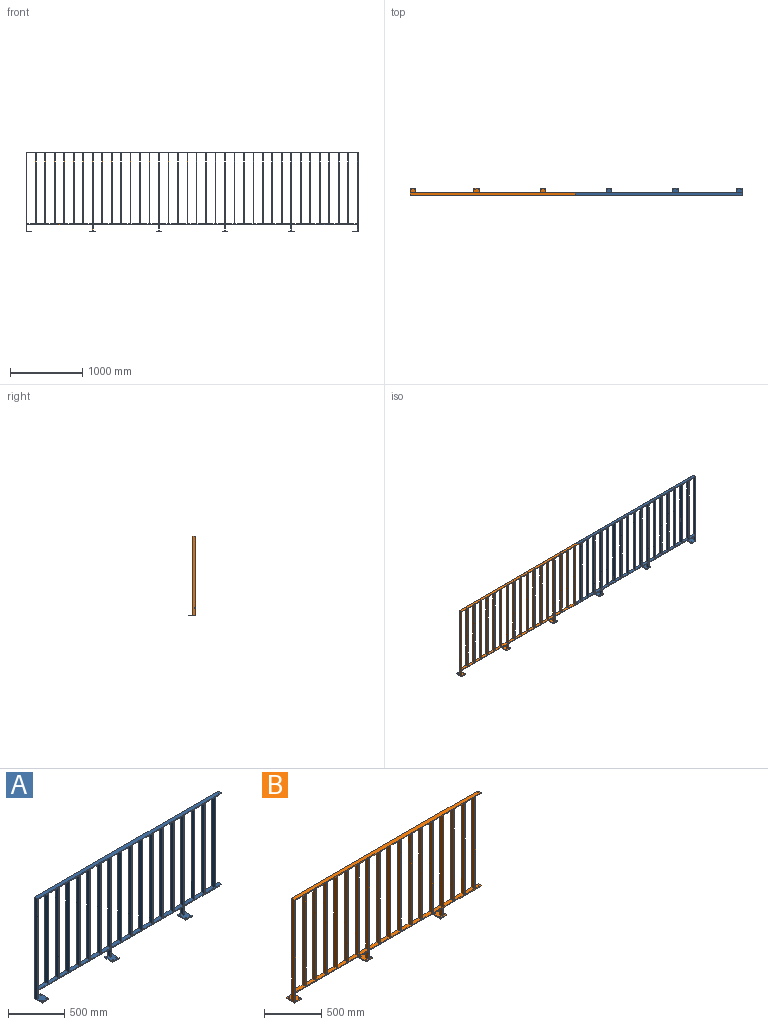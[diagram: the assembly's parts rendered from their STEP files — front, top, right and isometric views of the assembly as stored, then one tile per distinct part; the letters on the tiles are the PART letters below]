
ASSEMBLY  parts=2 mates=1
PART A: 114 faces, bbox 2304x100x1100 mm
  f0: plane 2304x1100mm, normal (0,1,0), area 227330mm2, adj f1,f2,f3,f4,f5,f6,f7,f8
  f1: plane 438x40mm, normal (0,0,-1), area 17520mm2, adj f0,f22,f83,f87
  f2: plane 906x40mm, normal (0,0,-1), area 36240mm2, adj f0,f22,f81,f84
  f3: plane 905x40mm, normal (0,0,-1), area 36200mm2, adj f0,f22,f80,f82
  f4: plane 120.8x40mm, normal (0,0,1), area 4832mm2, adj f0,f22,f58,f59
  f5: plane 120.8x40mm, normal (0,0,1), area 4832mm2, adj f0,f22,f56,f57
  f6: plane 120.8x40mm, normal (0,0,1), area 4832mm2, adj f0,f22,f54,f55
  f7: plane 120.8x40mm, normal (0,0,1), area 4832mm2, adj f0,f22,f52,f53
  f8: plane 120.8x40mm, normal (0,0,1), area 4832mm2, adj f0,f22,f48,f49
  f9: plane 120.8x40mm, normal (0,0,1), area 4832mm2, adj f0,f22,f46,f47
  f10: plane 120.8x40mm, normal (0,0,1), area 4832mm2, adj f0,f22,f44,f45
  f11: plane 120.8x40mm, normal (0,0,1), area 4832mm2, adj f0,f22,f42,f43
  f12: plane 120.8x40mm, normal (0,0,1), area 4832mm2, adj f0,f22,f40,f41
  f13: plane 120.8x40mm, normal (0,0,1), area 4832mm2, adj f0,f22,f38,f39
  f14: plane 120.8x40mm, normal (0,0,1), area 4832mm2, adj f0,f22,f36,f37
  f15: plane 120.8x40mm, normal (0,0,1), area 4832mm2, adj f0,f22,f34,f35
  f16: plane 120.8x40mm, normal (0,0,1), area 4832mm2, adj f0,f22,f25,f33
  f17: plane 70.4x40mm, normal (0,0,1), area 2816mm2, adj f0,f22,f23,f32
  f18: plane 120.8x40mm, normal (0,0,1), area 4832mm2, adj f0,f22,f30,f31
  f19: plane 120.8x40mm, normal (0,0,1), area 4832mm2, adj f0,f22,f28,f29
  f20: plane 120.8x40mm, normal (0,0,1), area 4832mm2, adj f0,f22,f26,f27
  f21: plane 1100x100mm, normal (-1,0,0), area 44600mm2, adj f0,f22,f78,f90,f91,f92
  f22: plane 2304x1090mm, normal (0,-1,0), area 224930mm2, adj f1,f2,f3,f4,f5,f6,f7,f8
  f23: plane 40x5mm, normal (1,0,0), area 200mm2, adj f0,f17,f22,f88
  f24: plane 120.8x40mm, normal (0,0,1), area 4832mm2, adj f0,f22,f50,f51
  f25: plane 980x40mm, normal (-1,0,0), area 39200mm2, adj f0,f16,f22,f60
  f26: plane 980x40mm, normal (1,0,0), area 39200mm2, adj f0,f20,f22,f61
  f27: plane 980x40mm, normal (-1,0,0), area 39200mm2, adj f0,f20,f22,f61
  f28: plane 980x40mm, normal (1,0,0), area 39200mm2, adj f0,f19,f22,f62
  f29: plane 980x40mm, normal (-1,0,0), area 39200mm2, adj f0,f19,f22,f62
  f30: plane 980x40mm, normal (1,0,0), area 39200mm2, adj f0,f18,f22,f63
  f31: plane 980x40mm, normal (-1,0,0), area 39200mm2, adj f0,f18,f22,f63
  f32: plane 980x40mm, normal (1,0,0), area 39200mm2, adj f0,f17,f22,f73
  f33: plane 980x40mm, normal (1,0,0), area 39200mm2, adj f0,f16,f22,f60
  f34: plane 980x40mm, normal (-1,0,0), area 39200mm2, adj f0,f15,f22,f64
  f35: plane 980x40mm, normal (1,0,0), area 39200mm2, adj f0,f15,f22,f64
  f36: plane 980x40mm, normal (-1,0,0), area 39200mm2, adj f0,f14,f22,f65
  f37: plane 980x40mm, normal (1,0,0), area 39200mm2, adj f0,f14,f22,f65
  f38: plane 980x40mm, normal (-1,0,0), area 39200mm2, adj f0,f13,f22,f66
  f39: plane 980x40mm, normal (1,0,0), area 39200mm2, adj f0,f13,f22,f66
  f40: plane 980x40mm, normal (-1,0,0), area 39200mm2, adj f0,f12,f22,f67
  f41: plane 980x40mm, normal (1,0,0), area 39200mm2, adj f0,f12,f22,f67
  f42: plane 980x40mm, normal (-1,0,0), area 39200mm2, adj f0,f11,f22,f68
  f43: plane 980x40mm, normal (1,0,0), area 39200mm2, adj f0,f11,f22,f68
  f44: plane 980x40mm, normal (-1,0,0), area 39200mm2, adj f0,f10,f22,f69
  f45: plane 980x40mm, normal (1,0,0), area 39200mm2, adj f0,f10,f22,f69
  f46: plane 980x40mm, normal (-1,0,0), area 39200mm2, adj f0,f9,f22,f70
  f47: plane 980x40mm, normal (1,0,0), area 39200mm2, adj f0,f9,f22,f70
  f48: plane 980x40mm, normal (-1,0,0), area 39200mm2, adj f0,f8,f22,f71
  f49: plane 980x40mm, normal (1,0,0), area 39200mm2, adj f0,f8,f22,f71
  f50: plane 980x40mm, normal (-1,0,0), area 39200mm2, adj f0,f22,f24,f72
  f51: plane 980x40mm, normal (1,0,0), area 39200mm2, adj f0,f22,f24,f72
  f52: plane 980x40mm, normal (-1,0,0), area 39200mm2, adj f0,f7,f22,f74
  f53: plane 980x40mm, normal (1,0,0), area 39200mm2, adj f0,f7,f22,f74
  f54: plane 980x40mm, normal (-1,0,0), area 39200mm2, adj f0,f6,f22,f75
  f55: plane 980x40mm, normal (1,0,0), area 39200mm2, adj f0,f6,f22,f75
  f56: plane 980x40mm, normal (-1,0,0), area 39200mm2, adj f0,f5,f22,f76
  f57: plane 980x40mm, normal (1,0,0), area 39200mm2, adj f0,f5,f22,f76
  f58: plane 980x40mm, normal (-1,0,0), area 39200mm2, adj f0,f4,f22,f79
  f59: plane 980x40mm, normal (1,0,0), area 39200mm2, adj f0,f4,f22,f79
  f60: plane 120.8x40mm, normal (0,0,-1), area 4832mm2, adj f0,f22,f25,f33
  f61: plane 120.8x40mm, normal (0,0,-1), area 4832mm2, adj f0,f22,f26,f27
  f62: plane 120.8x40mm, normal (0,0,-1), area 4832mm2, adj f0,f22,f28,f29
  f63: plane 120.8x40mm, normal (0,0,-1), area 4832mm2, adj f0,f22,f30,f31
  f64: plane 120.8x40mm, normal (0,0,-1), area 4832mm2, adj f0,f22,f34,f35
  f65: plane 120.8x40mm, normal (0,0,-1), area 4832mm2, adj f0,f22,f36,f37
  f66: plane 120.8x40mm, normal (0,0,-1), area 4832mm2, adj f0,f22,f38,f39
  f67: plane 120.8x40mm, normal (0,0,-1), area 4832mm2, adj f0,f22,f40,f41
  f68: plane 120.8x40mm, normal (0,0,-1), area 4832mm2, adj f0,f22,f42,f43
  f69: plane 120.8x40mm, normal (0,0,-1), area 4832mm2, adj f0,f22,f44,f45
  f70: plane 120.8x40mm, normal (0,0,-1), area 4832mm2, adj f0,f22,f46,f47
  f71: plane 120.8x40mm, normal (0,0,-1), area 4832mm2, adj f0,f22,f48,f49
  f72: plane 120.8x40mm, normal (0,0,-1), area 4832mm2, adj f0,f22,f50,f51
  f73: plane 45.4x40mm, normal (0,0,-1), area 1816mm2, adj f0,f22,f32,f85
  f74: plane 120.8x40mm, normal (0,0,-1), area 4832mm2, adj f0,f22,f52,f53
  f75: plane 120.8x40mm, normal (0,0,-1), area 4832mm2, adj f0,f22,f54,f55
  f76: plane 120.8x40mm, normal (0,0,-1), area 4832mm2, adj f0,f22,f56,f57
  f77: plane 40x5mm, normal (1,0,0), area 200mm2, adj f0,f22,f78,f86
  f78: plane 2304x40mm, normal (0,0,1), area 92160mm2, adj f0,f21,f22,f77
  f79: plane 120.8x40mm, normal (0,0,-1), area 4832mm2, adj f0,f22,f58,f59
  f80: plane 90x40mm, normal (1,0,0), area 3600mm2, adj f0,f3,f22,f92
  f81: plane 90x40mm, normal (1,0,0), area 3600mm2, adj f0,f2,f22,f97
  f82: plane 90x40mm, normal (-1,0,0), area 3600mm2, adj f0,f3,f22,f97
  f83: plane 90x40mm, normal (1,0,0), area 3600mm2, adj f0,f1,f22,f102
  f84: plane 90x40mm, normal (-1,0,0), area 3600mm2, adj f0,f2,f22,f102
  f85: plane 40x5mm, normal (1,0,0), area 200mm2, adj f0,f22,f73,f86
  f86: plane 40x25mm, normal (0,0,-1), area 1000mm2, adj f0,f22,f77,f85
  f87: plane 40x5mm, normal (1,0,0), area 200mm2, adj f0,f1,f22,f88
  f88: plane 40x25mm, normal (0,0,-1), area 1000mm2, adj f0,f22,f23,f87
  f89: plane 100x10mm, normal (1,0,0), area 1000mm2, adj f0,f90,f91,f92
  f90: plane 80x10mm, normal (0,-1,0), area 800mm2, adj f21,f89,f91,f92
  f91: plane 100x80mm, normal (0,0,-1), area 7660.7mm2, adj f0,f21,f89,f90,f103,f104,f105
  f92: plane 100x80mm, normal (0,0,1), area 7260.7mm2, adj f0,f21,f22,f80,f89,f90,f103,f104
  f93: plane 100x10mm, normal (1,0,0), area 1000mm2, adj f0,f94,f96,f97
  f94: plane 80x10mm, normal (0,-1,0), area 800mm2, adj f93,f95,f96,f97
  f95: plane 100x10mm, normal (-1,0,0), area 1000mm2, adj f0,f94,f96,f97
  f96: plane 100x80mm, normal (0,0,-1), area 7547.6mm2, adj f0,f93,f94,f95,f106,f107,f108,f109
  f97: plane 100x80mm, normal (0,0,1), area 7147.6mm2, adj f0,f22,f81,f82,f93,f94,f95,f106
  f98: plane 100x10mm, normal (1,0,0), area 1000mm2, adj f0,f99,f101,f102
  f99: plane 80x10mm, normal (0,-1,0), area 800mm2, adj f98,f100,f101,f102
  f100: plane 100x10mm, normal (-1,0,0), area 1000mm2, adj f0,f99,f101,f102
  f101: plane 100x80mm, normal (0,0,-1), area 7555.2mm2, adj f0,f98,f99,f100,f110,f111,f112,f113
  f102: plane 100x80mm, normal (0,0,1), area 7155.2mm2, adj f0,f22,f83,f84,f98,f99,f100,f110
  f103: cylinder r=6mm len=12mm, axis (0,0,-1), area 377mm2, adj f91,f92
  f104: cylinder r=6mm len=12mm, axis (0,0,-1), area 377mm2, adj f91,f92
  f105: cylinder r=6mm len=12mm, axis (0,0,-1), area 377mm2, adj f91,f92
  f106: cylinder r=6mm len=12mm, axis (0,0,-1), area 377mm2, adj f96,f97
  f107: cylinder r=6mm len=12mm, axis (0,0,-1), area 377mm2, adj f96,f97
  f108: cylinder r=6mm len=12mm, axis (0,0,-1), area 377mm2, adj f96,f97
  f109: cylinder r=6mm len=12mm, axis (0,0,-1), area 377mm2, adj f96,f97
  f110: cylinder r=5.9mm len=11.8mm, axis (0,0,-1), area 370.6mm2, adj f101,f102
  f111: cylinder r=5.9mm len=11.8mm, axis (0,0,-1), area 370.6mm2, adj f101,f102
  f112: cylinder r=6mm len=12mm, axis (0,0,-1), area 377mm2, adj f101,f102
  f113: cylinder r=6mm len=12mm, axis (0,0,-1), area 377mm2, adj f101,f102
PART B: 114 faces, bbox 2304x100x1100 mm
  f0: plane 2304x1090mm, normal (0,1,0), area 224930mm2, adj f1,f2,f3,f4,f5,f6,f7,f8
  f1: plane 40x5mm, normal (1,0,0), area 200mm2, adj f0,f23,f25,f113
  f2: plane 40x5mm, normal (1,0,0), area 200mm2, adj f0,f23,f74,f111
  f3: plane 905x40mm, normal (0,0,-1), area 36200mm2, adj f0,f23,f81,f84
  f4: plane 905x40mm, normal (0,0,-1), area 36200mm2, adj f0,f23,f80,f82
  f5: plane 120.8x40mm, normal (0,0,1), area 4832mm2, adj f0,f23,f59,f60
  f6: plane 120.8x40mm, normal (0,0,1), area 4832mm2, adj f0,f23,f57,f58
  f7: plane 120.8x40mm, normal (0,0,1), area 4832mm2, adj f0,f23,f55,f56
  f8: plane 120.8x40mm, normal (0,0,1), area 4832mm2, adj f0,f23,f53,f54
  f9: plane 120.8x40mm, normal (0,0,1), area 4832mm2, adj f0,f23,f49,f50
  f10: plane 120.8x40mm, normal (0,0,1), area 4832mm2, adj f0,f23,f47,f48
  f11: plane 120.8x40mm, normal (0,0,1), area 4832mm2, adj f0,f23,f45,f46
  f12: plane 120.8x40mm, normal (0,0,1), area 4832mm2, adj f0,f23,f43,f44
  f13: plane 120.8x40mm, normal (0,0,1), area 4832mm2, adj f0,f23,f41,f42
  f14: plane 120.8x40mm, normal (0,0,1), area 4832mm2, adj f0,f23,f39,f40
  f15: plane 120.8x40mm, normal (0,0,1), area 4832mm2, adj f0,f23,f37,f38
  f16: plane 120.8x40mm, normal (0,0,1), area 4832mm2, adj f0,f23,f35,f36
  f17: plane 120.8x40mm, normal (0,0,1), area 4832mm2, adj f0,f23,f26,f34
  f18: plane 45.4x40mm, normal (0,0,1), area 1816mm2, adj f0,f23,f33,f112
  f19: plane 120.8x40mm, normal (0,0,1), area 4832mm2, adj f0,f23,f31,f32
  f20: plane 120.8x40mm, normal (0,0,1), area 4832mm2, adj f0,f23,f29,f30
  f21: plane 120.8x40mm, normal (0,0,1), area 4832mm2, adj f0,f23,f27,f28
  f22: plane 1100x100mm, normal (-1,0,0), area 44600mm2, adj f0,f23,f78,f86,f87,f88
  f23: plane 2304x1100mm, normal (0,-1,0), area 227330mm2, adj f1,f2,f3,f4,f5,f6,f7,f8
  f24: plane 120.8x40mm, normal (0,0,1), area 4832mm2, adj f0,f23,f51,f52
  f25: plane 464x40mm, normal (0,0,-1), area 18560mm2, adj f0,f1,f23,f83
  f26: plane 980x40mm, normal (-1,0,0), area 39200mm2, adj f0,f17,f23,f61
  f27: plane 980x40mm, normal (1,0,0), area 39200mm2, adj f0,f21,f23,f62
  f28: plane 980x40mm, normal (-1,0,0), area 39200mm2, adj f0,f21,f23,f62
  f29: plane 980x40mm, normal (1,0,0), area 39200mm2, adj f0,f20,f23,f63
  f30: plane 980x40mm, normal (-1,0,0), area 39200mm2, adj f0,f20,f23,f63
  f31: plane 980x40mm, normal (1,0,0), area 39200mm2, adj f0,f19,f23,f64
  f32: plane 980x40mm, normal (-1,0,0), area 39200mm2, adj f0,f19,f23,f64
  f33: plane 980x40mm, normal (1,0,0), area 39200mm2, adj f0,f18,f23,f74
  f34: plane 980x40mm, normal (1,0,0), area 39200mm2, adj f0,f17,f23,f61
  f35: plane 980x40mm, normal (-1,0,0), area 39200mm2, adj f0,f16,f23,f65
  f36: plane 980x40mm, normal (1,0,0), area 39200mm2, adj f0,f16,f23,f65
  f37: plane 980x40mm, normal (-1,0,0), area 39200mm2, adj f0,f15,f23,f66
  f38: plane 980x40mm, normal (1,0,0), area 39200mm2, adj f0,f15,f23,f66
  f39: plane 980x40mm, normal (-1,0,0), area 39200mm2, adj f0,f14,f23,f67
  f40: plane 980x40mm, normal (1,0,0), area 39200mm2, adj f0,f14,f23,f67
  f41: plane 980x40mm, normal (-1,0,0), area 39200mm2, adj f0,f13,f23,f68
  f42: plane 980x40mm, normal (1,0,0), area 39200mm2, adj f0,f13,f23,f68
  f43: plane 980x40mm, normal (-1,0,0), area 39200mm2, adj f0,f12,f23,f69
  f44: plane 980x40mm, normal (1,0,0), area 39200mm2, adj f0,f12,f23,f69
  f45: plane 980x40mm, normal (-1,0,0), area 39200mm2, adj f0,f11,f23,f70
  f46: plane 980x40mm, normal (1,0,0), area 39200mm2, adj f0,f11,f23,f70
  f47: plane 980x40mm, normal (-1,0,0), area 39200mm2, adj f0,f10,f23,f71
  f48: plane 980x40mm, normal (1,0,0), area 39200mm2, adj f0,f10,f23,f71
  f49: plane 980x40mm, normal (-1,0,0), area 39200mm2, adj f0,f9,f23,f72
  f50: plane 980x40mm, normal (1,0,0), area 39200mm2, adj f0,f9,f23,f72
  f51: plane 980x40mm, normal (-1,0,0), area 39200mm2, adj f0,f23,f24,f73
  f52: plane 980x40mm, normal (1,0,0), area 39200mm2, adj f0,f23,f24,f73
  f53: plane 980x40mm, normal (-1,0,0), area 39200mm2, adj f0,f8,f23,f75
  f54: plane 980x40mm, normal (1,0,0), area 39200mm2, adj f0,f8,f23,f75
  f55: plane 980x40mm, normal (-1,0,0), area 39200mm2, adj f0,f7,f23,f76
  f56: plane 980x40mm, normal (1,0,0), area 39200mm2, adj f0,f7,f23,f76
  f57: plane 980x40mm, normal (-1,0,0), area 39200mm2, adj f0,f6,f23,f77
  f58: plane 980x40mm, normal (1,0,0), area 39200mm2, adj f0,f6,f23,f77
  f59: plane 980x40mm, normal (-1,0,0), area 39200mm2, adj f0,f5,f23,f79
  f60: plane 980x40mm, normal (1,0,0), area 39200mm2, adj f0,f5,f23,f79
  f61: plane 120.8x40mm, normal (0,0,-1), area 4832mm2, adj f0,f23,f26,f34
  f62: plane 120.8x40mm, normal (0,0,-1), area 4832mm2, adj f0,f23,f27,f28
  f63: plane 120.8x40mm, normal (0,0,-1), area 4832mm2, adj f0,f23,f29,f30
  f64: plane 120.8x40mm, normal (0,0,-1), area 4832mm2, adj f0,f23,f31,f32
  f65: plane 120.8x40mm, normal (0,0,-1), area 4832mm2, adj f0,f23,f35,f36
  f66: plane 120.8x40mm, normal (0,0,-1), area 4832mm2, adj f0,f23,f37,f38
  f67: plane 120.8x40mm, normal (0,0,-1), area 4832mm2, adj f0,f23,f39,f40
  f68: plane 120.8x40mm, normal (0,0,-1), area 4832mm2, adj f0,f23,f41,f42
  f69: plane 120.8x40mm, normal (0,0,-1), area 4832mm2, adj f0,f23,f43,f44
  f70: plane 120.8x40mm, normal (0,0,-1), area 4832mm2, adj f0,f23,f45,f46
  f71: plane 120.8x40mm, normal (0,0,-1), area 4832mm2, adj f0,f23,f47,f48
  f72: plane 120.8x40mm, normal (0,0,-1), area 4832mm2, adj f0,f23,f49,f50
  f73: plane 120.8x40mm, normal (0,0,-1), area 4832mm2, adj f0,f23,f51,f52
  f74: plane 70.4x40mm, normal (0,0,-1), area 2816mm2, adj f0,f2,f23,f33
  f75: plane 120.8x40mm, normal (0,0,-1), area 4832mm2, adj f0,f23,f53,f54
  f76: plane 120.8x40mm, normal (0,0,-1), area 4832mm2, adj f0,f23,f55,f56
  f77: plane 120.8x40mm, normal (0,0,-1), area 4832mm2, adj f0,f23,f57,f58
  f78: plane 2279x40mm, normal (0,0,1), area 91160mm2, adj f0,f22,f23,f110
  f79: plane 120.8x40mm, normal (0,0,-1), area 4832mm2, adj f0,f23,f59,f60
  f80: plane 90x40mm, normal (1,0,0), area 3600mm2, adj f0,f4,f23,f88
  f81: plane 90x40mm, normal (1,0,0), area 3600mm2, adj f0,f3,f23,f93
  f82: plane 90x40mm, normal (-1,0,0), area 3600mm2, adj f0,f4,f23,f93
  f83: plane 90x40mm, normal (1,0,0), area 3600mm2, adj f0,f23,f25,f98
  f84: plane 90x40mm, normal (-1,0,0), area 3600mm2, adj f0,f3,f23,f98
  f85: plane 100x10mm, normal (1,0,0), area 1000mm2, adj f23,f86,f87,f88
  f86: plane 80x10mm, normal (0,1,0), area 800mm2, adj f22,f85,f87,f88
  f87: plane 100x80mm, normal (0,0,-1), area 7660.7mm2, adj f22,f23,f85,f86,f99,f100,f101
  f88: plane 100x80mm, normal (0,0,1), area 7260.7mm2, adj f0,f22,f23,f80,f85,f86,f99,f100
  f89: plane 100x10mm, normal (-1,0,0), area 1000mm2, adj f23,f90,f92,f93
  f90: plane 80x10mm, normal (0,1,0), area 800mm2, adj f89,f91,f92,f93
  f91: plane 100x10mm, normal (1,0,0), area 1000mm2, adj f23,f90,f92,f93
  f92: plane 100x80mm, normal (0,0,-1), area 7547.6mm2, adj f23,f89,f90,f91,f102,f103,f104,f105
  f93: plane 100x80mm, normal (0,0,1), area 7147.6mm2, adj f0,f23,f81,f82,f89,f90,f91,f102
  f94: plane 100x10mm, normal (1,0,0), area 1000mm2, adj f23,f96,f97,f98
  f95: plane 100x10mm, normal (-1,0,0), area 1000mm2, adj f23,f96,f97,f98
  f96: plane 80x10mm, normal (0,1,0), area 800mm2, adj f94,f95,f97,f98
  f97: plane 100x80mm, normal (0,0,-1), area 7547.6mm2, adj f23,f94,f95,f96,f106,f107,f108,f109
  f98: plane 100x80mm, normal (0,0,1), area 7147.6mm2, adj f0,f23,f83,f84,f94,f95,f96,f106
  f99: cylinder r=6mm len=12mm, axis (0,0,-1), area 377mm2, adj f87,f88
  f100: cylinder r=6mm len=12mm, axis (0,0,-1), area 377mm2, adj f87,f88
  f101: cylinder r=6mm len=12mm, axis (0,0,-1), area 377mm2, adj f87,f88
  f102: cylinder r=6mm len=12mm, axis (0,0,-1), area 377mm2, adj f92,f93
  f103: cylinder r=6mm len=12mm, axis (0,0,-1), area 377mm2, adj f92,f93
  f104: cylinder r=6mm len=12mm, axis (0,0,-1), area 377mm2, adj f92,f93
  f105: cylinder r=6mm len=12mm, axis (0,0,-1), area 377mm2, adj f92,f93
  f106: cylinder r=6mm len=12mm, axis (0,0,-1), area 377mm2, adj f97,f98
  f107: cylinder r=6mm len=12mm, axis (0,0,-1), area 377mm2, adj f97,f98
  f108: cylinder r=6mm len=12mm, axis (0,0,-1), area 377mm2, adj f97,f98
  f109: cylinder r=6mm len=12mm, axis (0,0,-1), area 377mm2, adj f97,f98
  f110: plane 40x5mm, normal (1,0,0), area 200mm2, adj f0,f23,f78,f111
  f111: plane 40x25mm, normal (0,0,1), area 1000mm2, adj f0,f2,f23,f110
  f112: plane 40x5mm, normal (1,0,0), area 200mm2, adj f0,f18,f23,f113
  f113: plane 40x25mm, normal (0,0,1), area 1000mm2, adj f0,f1,f23,f112
PLACE A rot(axis=(0,0,1),180deg) t=(547.87,-588.15,-393.02)mm
PLACE B rot(axis=(0,0,-1),0deg) t=(-1731.13,-588.15,-393.02)mm
MATE fastened B.f111 <-> A.f86  axis (0,0,1) through (-591.63,-588.15,601.98)mm
